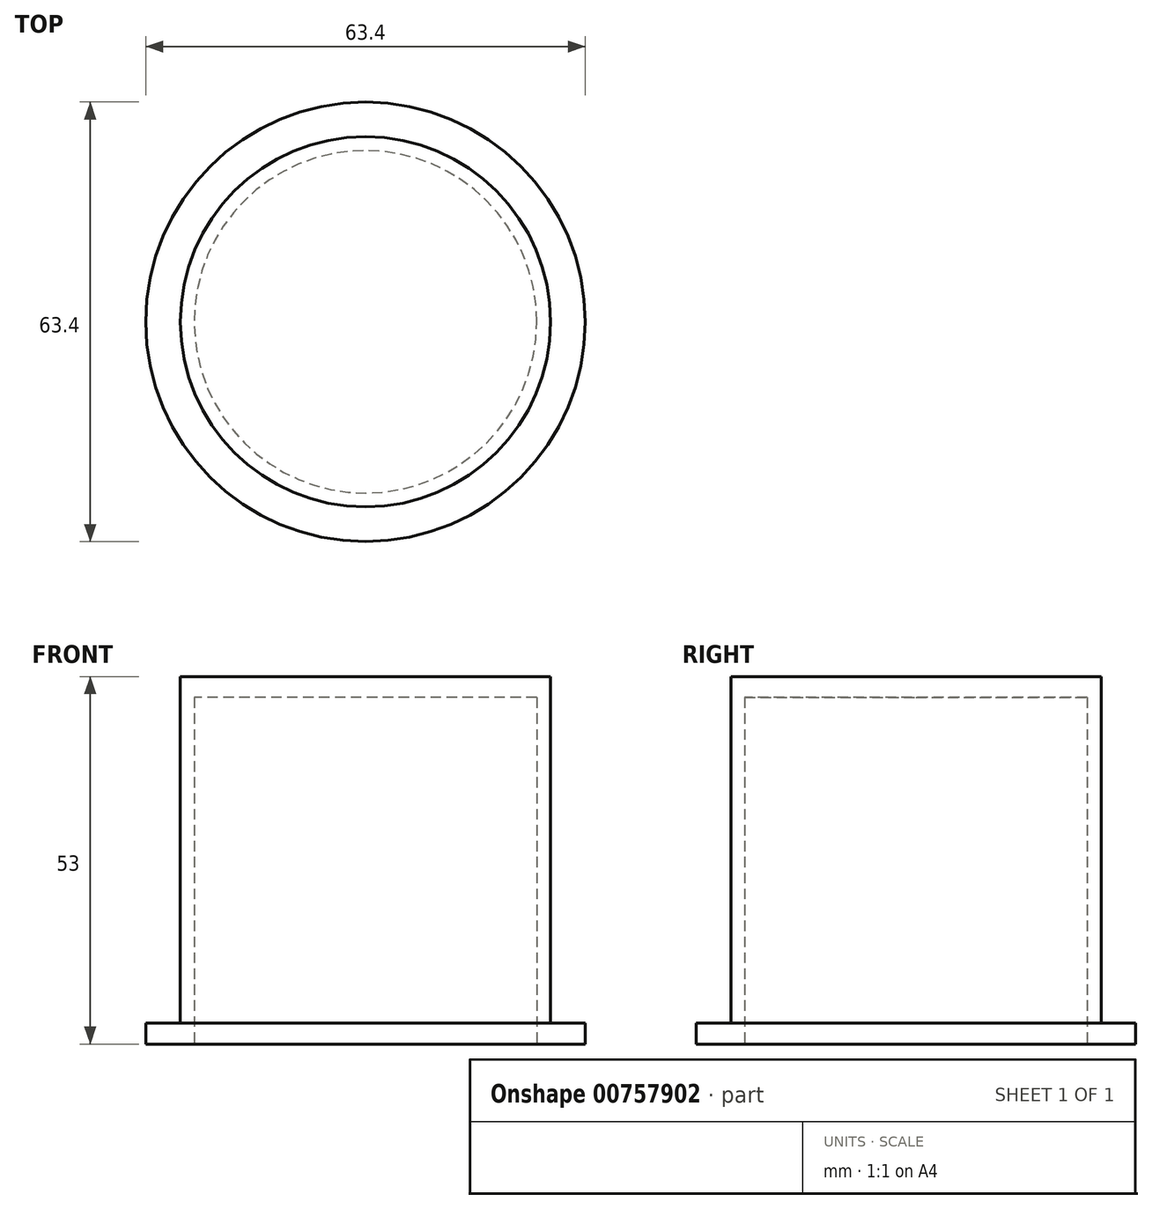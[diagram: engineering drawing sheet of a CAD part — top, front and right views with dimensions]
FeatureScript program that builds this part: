
annotation { "Feature Type Name" : "Feature", "Feature Type Description" : "" }
export const myFeature = defineFeature(function(context is Context, id is Id, definition is map)
    precondition{}
    {
        {
            var Q0;
            Q0=qCreatedBy(makeId("Top.planeOp"),FACE);
            var sketch = newSketch(context, id + "F0", { "sketchPlane" : qUnion([Q0])});
            skCircle(sketch, "E0", {"center": v(0, 0) * mm, "radius": 26.7 * mm});
            skCircle(sketch, "E1", {"center": v(0, 0) * mm, "radius": 24.7 * mm});
            skSolve(sketch);
        }
        {
            var Q0;
            Q0=makeQuery(id+"F0.imprint","IMPRINT",FACE,{"disambiguationData":[TD([[makeQuery(id+"F0.imprint","IMPRINT",EDGE,{"derivedFrom":sQuery(id+"F0.wireOp",EDGE,"E0")}),1.0]])]});
            extrude(context, id + "F1", {"entities" : qUnion([Q0]), "depth" : 50 * mm, "offsetDistance" : 25 * mm});
        }
        {
            var Q0;
            Q0=makeQuery(id+"F1.opExtrude","CAP_FACE",FACE,{"disambiguationData":[OSD([sQuery(id+"F0.wireOp",EDGE,"E0"),sQuery(id+"F0.wireOp",EDGE,"E1")])],"isStart":false});
            var sketch = newSketch(context, id + "F2", { "sketchPlane" : qUnion([Q0])});
            skCircle(sketch, "E2.0", {"center": v(0, 0) * mm, "radius": 26.7 * mm});
            skSolve(sketch);
        }
        {
            var Q0;
            Q0 = qSketchRegion(id + "F2", true);
            extrude(context, id + "F3", {"entities" : qUnion([Q0]), "operationType" : NewBodyOperationType.ADD, "depth" : 3 * mm, "offsetDistance" : 25 * mm});
        }
        {
            var Q0;
            Q0=makeQuery(id+"F1.opExtrude","CAP_FACE",FACE,{"disambiguationData":[OSD([sQuery(id+"F0.wireOp",EDGE,"E0"),sQuery(id+"F0.wireOp",EDGE,"E1")])],"isStart":true});
            var sketch = newSketch(context, id + "F4", { "sketchPlane" : qUnion([Q0])});
            skCircle(sketch, "E3.0", {"center": v(0, 0) * mm, "radius": 26.7 * mm});
            skCircle(sketch, "E4", {"center": v(0, 0) * mm, "radius": 31.7 * mm});
            skSolve(sketch);
        }
        {
            var Q0;
            Q0=makeQuery(id+"F4.imprint","IMPRINT",FACE,{"disambiguationData":[TD([[makeQuery(id+"F4.imprint","IMPRINT",EDGE,{"derivedFrom":sQuery(id+"F4.wireOp",EDGE,"E3.0")}),1.0]])]});
            extrude(context, id + "F5", {"entities" : qUnion([Q0]), "operationType" : NewBodyOperationType.ADD, "oppositeDirection" : true, "depth" : 3 * mm, "offsetDistance" : 25 * mm});
        }
    });
